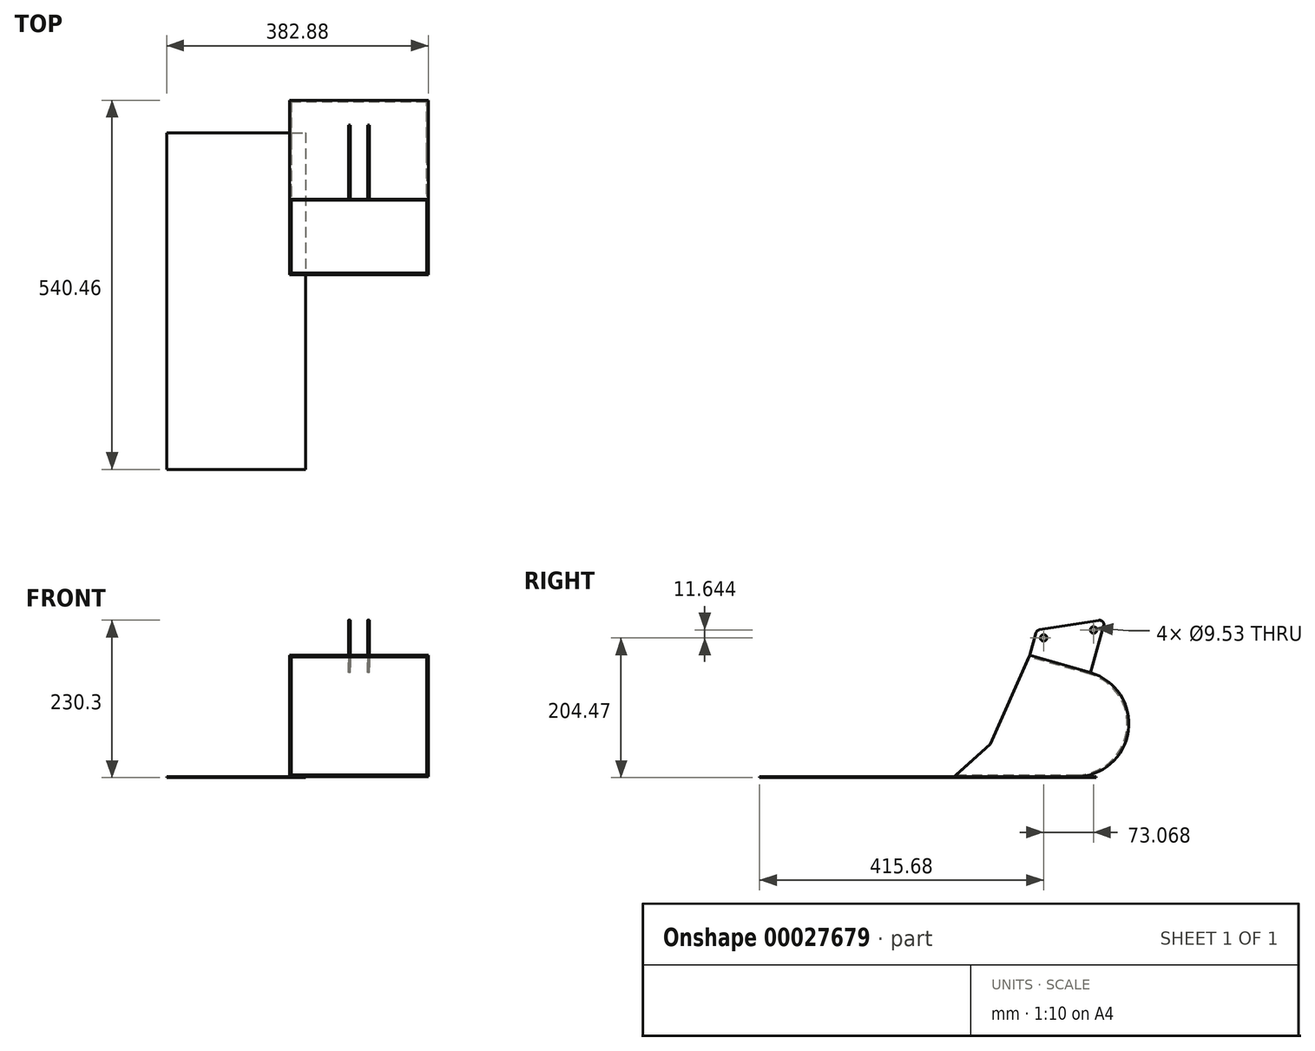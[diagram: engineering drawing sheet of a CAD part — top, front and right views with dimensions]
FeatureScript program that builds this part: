
annotation { "Feature Type Name" : "Feature", "Feature Type Description" : "" }
export const myFeature = defineFeature(function(context is Context, id is Id, definition is map)
    precondition{}
    {
        {
            var Q0;
            Q0=qCreatedBy(makeId("Right.planeOp"),FACE);
            var sketch = newSketch(context, id + "F0", { "sketchPlane" : qUnion([Q0])});
            skLineSegment(sketch, "E0", {"start": v(0, 0) * mm, "end": v(177.8, 0) * mm});
            skArc(sketch, "E1", {"start": v(177.8, 0) * mm, "mid": v(254.74, 66.92) * mm, "end": v(199.14, 152.4) * mm});
            skLineSegment(sketch, "E2", {"start": v(199.14, 152.4) * mm, "end": v(110.24, 177.8) * mm});
            skLineSegment(sketch, "E3", {"start": v(110.24, 177.8) * mm, "end": v(52.76, 47.7) * mm});
            skLineSegment(sketch, "E4", {"start": v(52.76, 47.7) * mm, "end": v(0, 0) * mm});
            skSolve(sketch);
        }
        {
            var Q0;
            Q0 = qSketchRegion(id + "F0", true);
            extrude(context, id + "F1", {"entities" : qUnion([Q0]), "offsetDistance" : 25.4 * mm, "depth" : 101.6 * mm, "hasSecondDirection" : true, "secondDirectionOppositeDirection" : true, "secondDirectionDepth" : 101.6 * mm});
        }
        {
            var Q0;
            Q0=makeQuery(id+"F1.opExtrude","SWEPT_FACE",FACE,{"disambiguationData":[OSD([sQuery(id+"F0.wireOp",EDGE,"E3")])]});
            var Q1;
            Q1=makeQuery(id+"F1.opExtrude","SWEPT_FACE",FACE,{"disambiguationData":[OSD([sQuery(id+"F0.wireOp",EDGE,"E4")])]});
            shell(context, id + "F2", {"entities" : qUnion([Q0, Q1]), "thickness" : 2.54 * mm});
        }
        {
            var Q0;
            Q0=makeQuery(id+"F1.opExtrude","SWEPT_FACE",FACE,{"disambiguationData":[OSD([sQuery(id+"F0.wireOp",EDGE,"E2")])]});
            var sketch = newSketch(context, id + "F3", { "sketchPlane" : qUnion([Q0])});
            skLineSegment(sketch, "E5.bottom", {"start": v(12.7, 149.61) * mm, "end": v(15.24, 149.61) * mm});
            skLineSegment(sketch, "E5.top", {"start": v(12.7, 57.16) * mm, "end": v(15.24, 57.16) * mm});
            skLineSegment(sketch, "E5.left", {"start": v(12.7, 149.61) * mm, "end": v(12.7, 57.16) * mm});
            skLineSegment(sketch, "E5.right", {"start": v(15.24, 149.61) * mm, "end": v(15.24, 57.16) * mm});
            skLineSegment(sketch, "E6", {"start": v(0, 57.16) * mm, "end": v(0, 149.61) * mm, "construction": true});
            skLineSegment(sketch, "E7.MirrorCS", {"start": v(-12.7, 149.61) * mm, "end": v(-15.24, 149.61) * mm});
            skLineSegment(sketch, "E8.MirrorCS", {"start": v(-12.7, 57.16) * mm, "end": v(-15.24, 57.16) * mm});
            skLineSegment(sketch, "E9.MirrorCS", {"start": v(-15.24, 149.61) * mm, "end": v(-15.24, 57.16) * mm});
            skLineSegment(sketch, "E10.MirrorCS", {"start": v(-12.7, 149.61) * mm, "end": v(-12.7, 57.16) * mm});
            skSolve(sketch);
        }
        {
            var Q0;
            Q0 = qSketchRegion(id + "F3", true);
            extrude(context, id + "F4", {"entities" : qUnion([Q0]), "operationType" : NewBodyOperationType.ADD, "depth" : 101.6 * mm});
        }
        {
            var Q0;
            Q0=makeQuery(id+"F4.opExtrude","SWEPT_FACE",FACE,{"disambiguationData":[OSD([sQuery(id+"F3.wireOp",EDGE,"E5.right")])]});
            var sketch = newSketch(context, id + "F5", { "sketchPlane" : qUnion([Q0])});
            skLineSegment(sketch, "E11.2", {"start": v(218.73, 220.94) * mm, "end": v(199.14, 152.4) * mm});
            skCircle(sketch, "E12", {"center": v(130.7, 203.2) * mm, "radius": 4.76 * mm});
            skCircle(sketch, "E13", {"center": v(203.78, 214.84) * mm, "radius": 4.76 * mm});
            skLineSegment(sketch, "E14", {"start": v(130.7, 203.2) * mm, "end": v(118.5, 206.69) * mm, "construction": true});
            skLineSegment(sketch, "E15", {"start": v(203.78, 214.84) * mm, "end": v(215.99, 211.36) * mm, "construction": true});
            skLineSegment(sketch, "E16", {"start": v(110.24, 177.8) * mm, "end": v(85.64, 191.22) * mm});
            skLineSegment(sketch, "E17", {"start": v(85.64, 191.22) * mm, "end": v(148.81, 350.16) * mm});
            skLineSegment(sketch, "E18", {"start": v(148.81, 350.16) * mm, "end": v(283.5, 317.6) * mm});
            skLineSegment(sketch, "E19", {"start": v(283.5, 317.6) * mm, "end": v(218.24, 151.44) * mm});
            skLineSegment(sketch, "E20", {"start": v(218.24, 151.44) * mm, "end": v(199.14, 152.4) * mm});
            skLineSegment(sketch, "E21", {"start": v(110.24, 177.8) * mm, "end": v(119.6, 210.58) * mm});
            skLineSegment(sketch, "E22", {"start": v(124.72, 215.1) * mm, "end": v(211.62, 228.95) * mm});
            skLineSegment(sketch, "E23", {"start": v(130.7, 203.2) * mm, "end": v(203.78, 214.84) * mm, "construction": true});
            skPoint(sketch, "E24.visualSharp", {"position": v(120.72, 214.47) * mm});
            skArc(sketch, "E24.filletArc", {"start": v(124.72, 215.1) * mm, "mid": v(121.5, 213.59) * mm, "end": v(119.6, 210.58) * mm});
            skPoint(sketch, "E25.visualSharp", {"position": v(221.47, 230.52) * mm});
            skArc(sketch, "E25.filletArc", {"start": v(218.73, 220.94) * mm, "mid": v(217.37, 226.9) * mm, "end": v(211.62, 228.95) * mm});
            skSolve(sketch);
        }
        {
            var Q0;
            Q0 = qSketchRegion(id + "F5", true);
            extrude(context, id + "F6", {"entities" : qUnion([Q0]), "operationType" : NewBodyOperationType.REMOVE, "endBound" : BoundingType.THROUGH_ALL, "oppositeDirection" : true, "depth" : 25.4 * mm});
        }
        {
            var Q0;
            Q0=makeQuery(id+"F1.opExtrude","SWEPT_FACE",FACE,{"disambiguationData":[OSD([sQuery(id+"F0.wireOp",EDGE,"E0")])]});
            var sketch = newSketch(context, id + "F7", { "sketchPlane" : qUnion([Q0])});
            skLineSegment(sketch, "E26", {"start": v(-78.08, 284.97) * mm, "end": v(-281.28, 284.97) * mm});
            skLineSegment(sketch, "E27", {"start": v(-281.28, 284.97) * mm, "end": v(-281.28, -207.8) * mm});
            skLineSegment(sketch, "E28", {"start": v(-281.28, -207.8) * mm, "end": v(-78.08, -207.8) * mm});
            skLineSegment(sketch, "E29", {"start": v(-78.08, -207.8) * mm, "end": v(-78.08, 284.97) * mm});
            skSolve(sketch);
        }
        {
            var Q0;
            Q0 = qSketchRegion(id + "F7", true);
            extrude(context, id + "F8", {"entities" : qUnion([Q0]), "depth" : 1.27 * mm});
        }
    });
